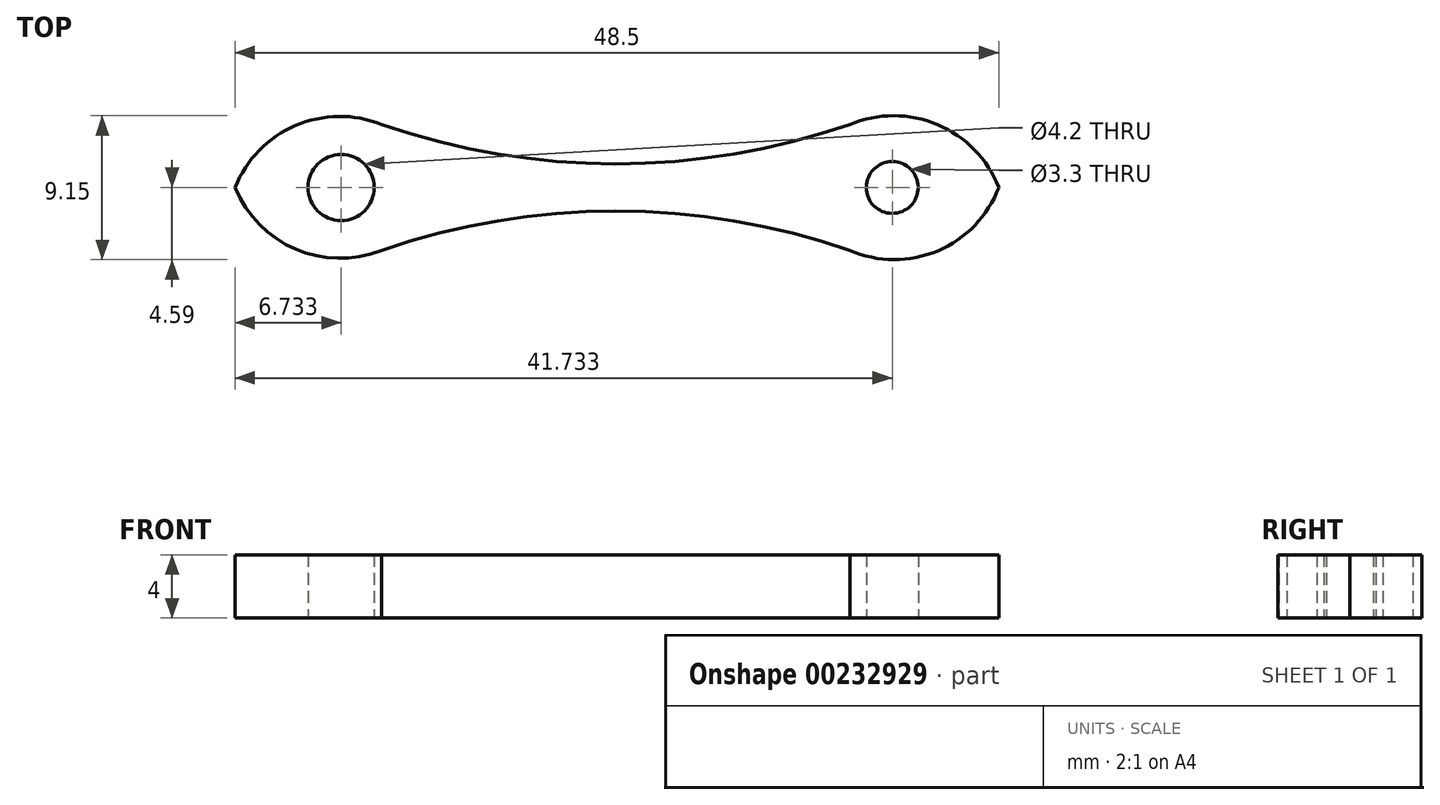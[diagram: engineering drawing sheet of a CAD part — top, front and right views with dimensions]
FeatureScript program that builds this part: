
annotation { "Feature Type Name" : "Feature", "Feature Type Description" : "" }
export const myFeature = defineFeature(function(context is Context, id is Id, definition is map)
    precondition{}
    {
        {
            var Q0;
            Q0=qCreatedBy(makeId("Top.planeOp"),FACE);
            var sketch = newSketch(context, id + "F0", { "sketchPlane" : qUnion([Q0])});
            skLineSegment(sketch, "E0.left", {"start": v(-24.25, 0) * mm, "end": v(-24.25, 0) * mm});
            skLineSegment(sketch, "E0.right", {"start": v(24.25, 0) * mm, "end": v(24.25, 0) * mm});
            skPoint(sketch, "E0.middle", {"position": v(0, 0) * mm});
            skCircle(sketch, "E1", {"center": v(17.48, 0) * mm, "radius": 1.65 * mm});
            skPoint(sketch, "E2", {"position": v(-17.52, 0) * mm});
            skCircle(sketch, "E3", {"center": v(-17.52, 0) * mm, "radius": 2.1 * mm});
            skPoint(sketch, "E4.visualSharp", {"position": v(-24.25, -4) * mm});
            skPoint(sketch, "E5.visualSharp", {"position": v(-24.25, 4) * mm});
            skArc(sketch, "E5.filletArc", {"start": v(-20.25, 4) * mm, "mid": v(-20.26, 4) * mm, "end": v(-20.26, 4) * mm});
            skPoint(sketch, "E6.visualSharp", {"position": v(24.25, -4) * mm});
            skArc(sketch, "E6.filletArc", {"start": v(20.25, -4) * mm, "mid": v(20.35, -4) * mm, "end": v(20.44, -4) * mm});
            skPoint(sketch, "E7", {"position": v(-14.95, -4) * mm});
            skPoint(sketch, "E8", {"position": v(14.78, -4) * mm});
            skPoint(sketch, "E9", {"position": v(0, -1.5) * mm});
            skPoint(sketch, "E10", {"position": v(0, 1.5) * mm});
            skArc(sketch, "E11", {"start": v(14.78, -4) * mm, "mid": v(-0.08, -1.5) * mm, "end": v(-14.95, -4) * mm});
            skArc(sketch, "E12", {"start": v(-14.95, 4) * mm, "mid": v(-0.08, 1.5) * mm, "end": v(14.78, 4) * mm});
            skArc(sketch, "E13", {"start": v(-14.95, 4) * mm, "mid": v(-20.43, 3.93) * mm, "end": v(-24.25, 0) * mm});
            skArc(sketch, "E14", {"start": v(-24.25, 0) * mm, "mid": v(-20.42, -3.91) * mm, "end": v(-14.95, -4) * mm});
            skPoint(sketch, "E15.visualSharp", {"position": v(24.25, 4) * mm});
            skArc(sketch, "E15.filletArc", {"start": v(20.33, 4) * mm, "mid": v(20.3, 4) * mm, "end": v(20.25, 4) * mm});
            skArc(sketch, "E16", {"start": v(24.25, 0) * mm, "mid": v(20.36, 3.99) * mm, "end": v(14.78, 4) * mm});
            skArc(sketch, "E17", {"start": v(14.78, -4) * mm, "mid": v(20.37, -4.03) * mm, "end": v(24.25, 0) * mm});
            skSolve(sketch);
        }
        {
            var Q0;
            Q0=makeQuery(id+"F0.imprint","IMPRINT",FACE,{"disambiguationData":[TD([[makeQuery(id+"F0.imprint","IMPRINT",EDGE,{"derivedFrom":sQuery(id+"F0.wireOp",EDGE,"E1")}),-1.0]])]});
            extrude(context, id + "F1", {"entities" : qUnion([Q0]), "depth" : 4 * mm});
        }
    });
